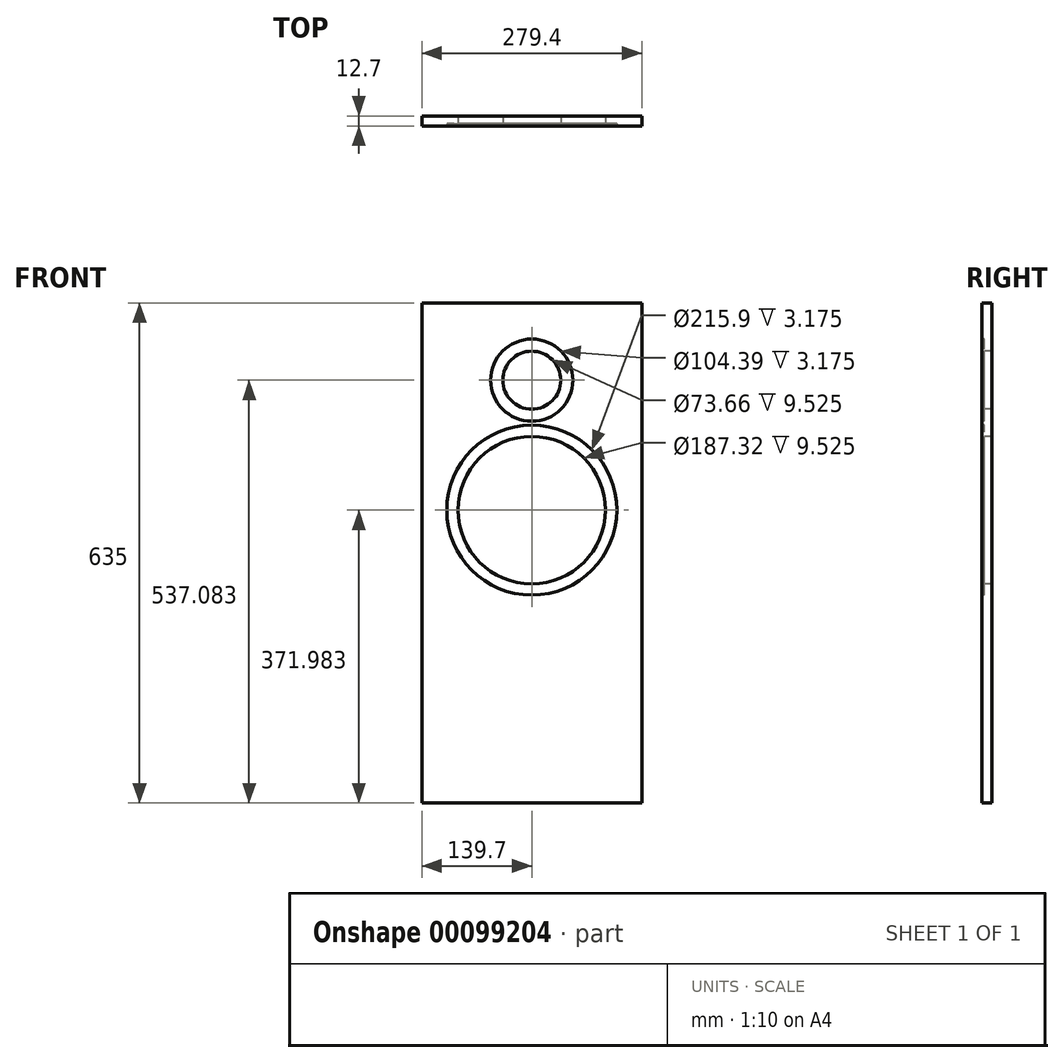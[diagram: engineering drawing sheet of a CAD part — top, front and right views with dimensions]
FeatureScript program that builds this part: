
annotation { "Feature Type Name" : "Feature", "Feature Type Description" : "" }
export const myFeature = defineFeature(function(context is Context, id is Id, definition is map)
    precondition{}
    {
        {
            var Q0;
            Q0=qCreatedBy(makeId("Front.planeOp"),FACE);
            var sketch = newSketch(context, id + "F0", { "sketchPlane" : qUnion([Q0])});
            skLineSegment(sketch, "E0.bottom", {"start": v(0, 635) * mm, "end": v(279.4, 635) * mm});
            skLineSegment(sketch, "E0.top", {"start": v(0, 0) * mm, "end": v(279.4, 0) * mm});
            skLineSegment(sketch, "E0.left", {"start": v(0, 635) * mm, "end": v(0, 0) * mm});
            skLineSegment(sketch, "E0.right", {"start": v(279.4, 635) * mm, "end": v(279.4, 0) * mm});
            skSolve(sketch);
        }
        {
            var Q0;
            Q0=makeQuery(id+"F0.imprint","IMPRINT",FACE,{"disambiguationData":[TD([[makeQuery(id+"F0.imprint","IMPRINT",EDGE,{"derivedFrom":sQuery(id+"F0.wireOp",EDGE,"E0.bottom")}),-1.0]])]});
            extrude(context, id + "F1", {"entities" : qUnion([Q0]), "depth" : 12.7 * mm});
        }
        {
            var Q0;
            Q0=makeQuery(id+"F1.opExtrude","CAP_FACE",FACE,{"disambiguationData":[OSD([sQuery(id+"F0.wireOp",EDGE,"E0.bottom"),sQuery(id+"F0.wireOp",EDGE,"E0.top"),sQuery(id+"F0.wireOp",EDGE,"E0.left"),sQuery(id+"F0.wireOp",EDGE,"E0.right")])],"isStart":false});
            var sketch = newSketch(context, id + "F2", { "sketchPlane" : qUnion([Q0])});
            skCircle(sketch, "E1", {"center": v(139.7, 371.98) * mm, "radius": 107.95 * mm});
            skPoint(sketch, "E1.centerSnap0", {"position": v(139.7, 0) * mm});
            skLineSegment(sketch, "E2", {"start": v(139.7, 0) * mm, "end": v(139.7, 371.98) * mm, "construction": true});
            skCircle(sketch, "E3", {"center": v(139.7, 537.08) * mm, "radius": 52.2 * mm});
            skLineSegment(sketch, "E4", {"start": v(139.7, 371.98) * mm, "end": v(139.7, 537.08) * mm, "construction": true});
            skLineSegment(sketch, "E5", {"start": v(139.7, 635) * mm, "end": v(139.7, 537.08) * mm, "construction": true});
            skSolve(sketch);
        }
        {
            var Q0;
            Q0=makeQuery(id+"F2.imprint","IMPRINT",FACE,{"disambiguationData":[TD([[makeQuery(id+"F2.imprint","IMPRINT",EDGE,{"derivedFrom":sQuery(id+"F2.wireOp",EDGE,"E3")}),1.0]])]});
            var Q1;
            Q1=makeQuery(id+"F2.imprint","IMPRINT",FACE,{"disambiguationData":[TD([[makeQuery(id+"F2.imprint","IMPRINT",EDGE,{"derivedFrom":sQuery(id+"F2.wireOp",EDGE,"E1")}),1.0]])]});
            extrude(context, id + "F3", {"entities" : qUnion([Q0, Q1]), "operationType" : NewBodyOperationType.REMOVE, "oppositeDirection" : true, "depth" : 3.17 * mm});
        }
        {
            var Q0;
            Q0=makeQuery(id+"F1.opExtrude","CAP_FACE",FACE,{"disambiguationData":[OSD([sQuery(id+"F0.wireOp",EDGE,"E0.bottom"),sQuery(id+"F0.wireOp",EDGE,"E0.top"),sQuery(id+"F0.wireOp",EDGE,"E0.left"),sQuery(id+"F0.wireOp",EDGE,"E0.right")])],"isStart":false});
            var sketch = newSketch(context, id + "F4", { "sketchPlane" : qUnion([Q0])});
            skCircle(sketch, "E6.0", {"center": v(139.7, 537.08) * mm, "radius": 52.2 * mm, "construction": true});
            skCircle(sketch, "E7.0", {"center": v(139.7, 371.98) * mm, "radius": 107.95 * mm, "construction": true});
            skCircle(sketch, "E8", {"center": v(139.7, 537.08) * mm, "radius": 36.83 * mm});
            skCircle(sketch, "E9", {"center": v(139.7, 371.98) * mm, "radius": 93.66 * mm});
            skSolve(sketch);
        }
        {
            var Q0;
            Q0=makeQuery(id+"F4.imprint","IMPRINT",FACE,{"disambiguationData":[TD([[makeQuery(id+"F4.imprint","IMPRINT",EDGE,{"derivedFrom":sQuery(id+"F4.wireOp",EDGE,"E8")}),1.0]])]});
            var Q1;
            Q1=makeQuery(id+"F4.imprint","IMPRINT",FACE,{"disambiguationData":[TD([[makeQuery(id+"F4.imprint","IMPRINT",EDGE,{"derivedFrom":sQuery(id+"F4.wireOp",EDGE,"E9")}),1.0]])]});
            extrude(context, id + "F5", {"entities" : qUnion([Q0, Q1]), "operationType" : NewBodyOperationType.REMOVE, "endBound" : BoundingType.THROUGH_ALL, "oppositeDirection" : true, "depth" : 25.4 * mm});
        }
    });
